# Revit family: STL22401BR_STL22401PTO
name_source: partatom
category: Luminárias
units: mm (PartAtom-declared; Revit-internal decimal feet)

## family parameters
Compartilhado = Não
Corte com vazios quando carregada = Não
Cota do conector redondo = Utilizar diâmetro
Fonte luminosa = Não
Hospedeiro = Forro
Manter orientação da anotação = Não
Número OmniClass = 23.80.70.11
Ponto de cálculo do ambiente = Não
Sempre na vertical = Sim
Tipo de parte = Normal
Título OmniClass = Luminaries for Internal Lighting

## types (2) — shared parameters
Altura = 0.05 m
Comprimento = 1.01 m
Fabricante = Stella
Grau de proteção (IP) = IP20
Largura = 0.05 m
Modelo = Trace - Trilho de Embutir 1m
Trace - Trilho de Sobrepor 2m
Potência máxima = 1000 W
Tensão Elétrica = 127V-220V
URL = https://stella.com.br
zero-valued in all types: Elevação padrão

## per-type parameters (varying)
| type | Estrutura |
| STL22401BR - BRANCO - 1m | Al - Branco |
| STL22401PTO - PRETO - 1m | Al - Preto |

note: column(s) folded — value = type name in every type: Referência
